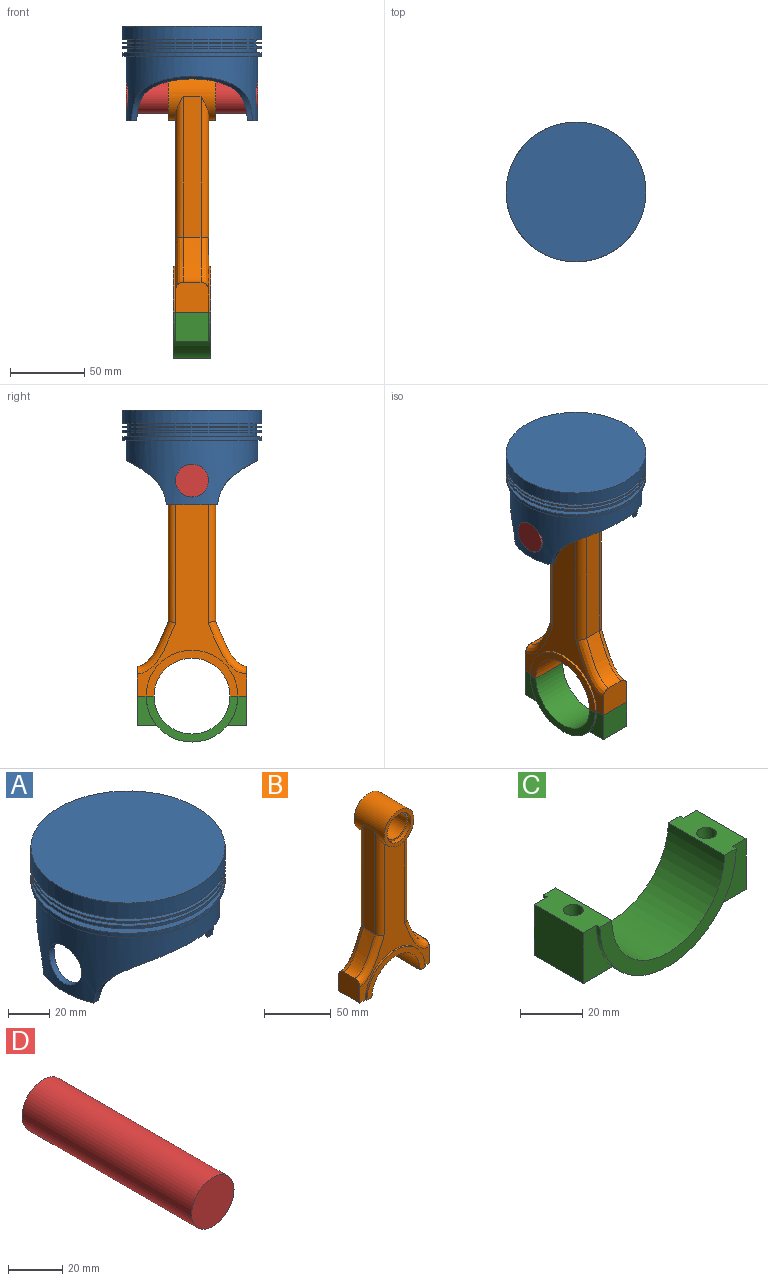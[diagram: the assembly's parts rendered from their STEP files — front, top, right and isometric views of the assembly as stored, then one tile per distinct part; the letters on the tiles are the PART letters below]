
ASSEMBLY  parts=4 mates=3
PART A: 24 faces, bbox 94x94x63.5 mm
  f0: cylinder r=44.12mm len=88.25mm, axis (0,0,1), area 6410.7mm2, adj f1,f2,f5,f20,f21,f22,f23
  f1: plane 34.12x6.9mm, normal (0,0,-1), area 111.5mm2, adj f0,f3,f20,f23
  f2: plane 34.12x6.9mm, normal (0,0,-1), area 111.5mm2, adj f0,f3,f20,f23
  f3: cylinder r=40.95mm len=81.9mm, axis (0,0,-1), area 9030.3mm2, adj f1,f2,f19,f20,f21,f22,f23
  f4: cylinder r=46.99mm len=93.98mm, axis (0,0,-1), area 712.8mm2, adj f5,f7
  f5: plane 93.98x93.98mm, normal (0,0,-1), area 820.3mm2, adj f0,f4
  f6: plane 93.98x93.98mm, normal (0,0,-1), area 1021.2mm2, adj f8,f9
  f7: plane 93.98x93.98mm, normal (0,0,1), area 1021.2mm2, adj f4,f8
  f8: cylinder r=43.39mm len=86.79mm, axis (0,0,-1), area 735mm2, adj f6,f7
  f9: cylinder r=46.99mm len=93.98mm, axis (0,0,-1), area 449.9mm2, adj f6,f11
  f10: plane 93.98x93.98mm, normal (0,0,-1), area 1021.2mm2, adj f12,f13
  f11: plane 93.98x93.98mm, normal (0,0,1), area 1021.2mm2, adj f9,f12
  f12: cylinder r=43.39mm len=86.79mm, axis (0,0,-1), area 463.4mm2, adj f10,f11
  f13: cylinder r=46.99mm len=93.98mm, axis (0,0,-1), area 328.8mm2, adj f10,f15
  f14: plane 93.98x93.98mm, normal (0,0,-1), area 1021.2mm2, adj f16,f18
  f15: plane 93.98x93.98mm, normal (0,0,1), area 1021.2mm2, adj f13,f16
  f16: cylinder r=43.39mm len=86.79mm, axis (0,0,-1), area 447.4mm2, adj f14,f15
  f17: plane 93.98x93.98mm, normal (0,0,1), area 6936.8mm2, adj f18
  f18: cylinder r=46.99mm len=93.98mm, axis (0,0,-1), area 2718.4mm2, adj f14,f17
  f19: plane 81.9x81.9mm, normal (0,0,-1), area 5268mm2, adj f3
  f20: extruded ~81.39x29.6mm, area 438.2mm2, adj f0,f1,f2,f3
  f21: cylinder r=11.01mm len=22.02mm, axis (1,0,0), area 223.6mm2, adj f0,f3
  f22: cylinder r=11.01mm len=22.02mm, axis (1,0,0), area 223.4mm2, adj f0,f3
  f23: extruded ~81.39x29.6mm, area 438.2mm2, adj f0,f1,f2,f3
PART B: 35 faces, bbox 79.2x31.9x160.8 mm
  f0: cylinder r=30.86mm len=61.72mm, axis (0,1,0), area 153.9mm2, adj f4,f12,f29,f30
  f1: cylinder r=12.7mm len=25.4mm, axis (0,1,0), area 253.4mm2, adj f17,f20
  f2: cylinder r=25.5mm len=51mm, axis (0,1,0), area 2034.3mm2, adj f4,f5,f29,f30
  f3: cylinder r=30.86mm len=61.72mm, axis (0,1,0), area 153.9mm2, adj f5,f13,f29,f30
  f4: plane 61.72x30.85mm, normal (0,-1,0), area 474.4mm2, adj f0,f2,f29,f30
  f5: plane 61.72x30.85mm, normal (0,1,0), area 474.4mm2, adj f2,f3,f29,f30
  f6: plane 94.46x12.07mm, normal (-1,0,0), area 1139.7mm2, adj f7,f15,f23,f27
  f7: extruded ~30.36x21.01mm, area 464.3mm2, adj f6,f8,f24,f28
  f8: plane 22.4x20.12mm, normal (-1,0,0), area 432.2mm2, adj f7,f12,f13,f24,f28,f29
  f9: plane 22.4x20.12mm, normal (1,0,0), area 432.2mm2, adj f10,f12,f13,f22,f26,f30
  f10: extruded ~30.36x21.01mm, area 464.3mm2, adj f9,f11,f22,f26
  f11: plane 94.46x12.07mm, normal (1,0,0), area 1139.7mm2, adj f10,f15,f21,f25
  f12: plane 133.13x73.78mm, normal (0,-1,0), area 2672.2mm2, adj f0,f8,f9,f15,f25,f26,f27,f28
  f13: plane 133.13x73.78mm, normal (0,1,0), area 2672.2mm2, adj f3,f8,f9,f15,f21,f22,f23,f24
  f14: cylinder r=12.7mm len=25.4mm, axis (0,1,0), area 253.4mm2, adj f16,f19
  f15: cylinder r=15.88mm len=31.75mm, axis (0,1,0), area 2191.2mm2, adj f6,f11,f12,f13,f16,f17,f21,f23
  f16: plane 31.75x31.75mm, normal (0,-1,0), area 285mm2, adj f14,f15
  f17: plane 31.75x31.75mm, normal (0,1,0), area 285mm2, adj f1,f15
  f18: cylinder r=11.01mm len=25.4mm, axis (0,1,0), area 1757.3mm2, adj f19,f20
  f19: plane 25.4x25.4mm, normal (0,-1,0), area 125.8mm2, adj f14,f18
  f20: plane 25.4x25.4mm, normal (0,1,0), area 125.8mm2, adj f1,f18
  f21: cylinder r=5.08mm len=95.44mm, axis (0,0,1), area 711.2mm2, adj f11,f13,f15,f22
  f22: bspline ~38.02x29.36mm, area 328.6mm2, adj f9,f10,f13,f21
  f23: cylinder r=5.08mm len=95.44mm, axis (0,0,-1), area 711.2mm2, adj f6,f13,f15,f24
  f24: bspline ~38.02x29.36mm, area 328.6mm2, adj f7,f8,f13,f23
  f25: cylinder r=5.08mm len=95.44mm, axis (0,0,-1), area 711.2mm2, adj f11,f12,f15,f26
  f26: bspline ~38.02x29.36mm, area 328.6mm2, adj f9,f10,f12,f25
  f27: cylinder r=5.08mm len=95.44mm, axis (0,0,1), area 711.2mm2, adj f6,f12,f15,f28
  f28: bspline ~38.02x29.36mm, area 328.6mm2, adj f7,f8,f12,f27
  f29: plane 25.4x11.38mm, normal (0,0,-1), area 238.3mm2, adj f0,f2,f3,f4,f5,f8,f12,f13
  f30: plane 25.4x11.38mm, normal (0,0,-1), area 238.3mm2, adj f0,f2,f3,f4,f5,f9,f12,f13
  f31: plane 6.35x6.35mm, normal (0,0,-1), area 31.7mm2, adj f32
  f32: cylinder r=3.17mm len=11.78mm, axis (0,0,-1), area 235mm2, adj f29,f31
  f33: plane 6.35x6.35mm, normal (0,0,-1), area 31.7mm2, adj f34
  f34: cylinder r=3.17mm len=11.78mm, axis (0,0,-1), area 235mm2, adj f30,f33
PART C: 16 faces, bbox 73.8x25.4x30.8 mm
  f0: plane 19.95x13.34mm, normal (0,1,0), area 166.2mm2, adj f2,f8,f12,f15
  f1: plane 19.95x13.34mm, normal (0,-1,0), area 166.2mm2, adj f2,f8,f12,f15
  f2: plane 22.23x19.95mm, normal (1,0,0), area 443.3mm2, adj f0,f1,f12,f15
  f3: plane 61.72x30.85mm, normal (0,1,0), area 474.4mm2, adj f8,f9,f14,f15
  f4: plane 19.95x13.34mm, normal (0,1,0), area 166.2mm2, adj f6,f8,f10,f14
  f5: plane 19.95x13.34mm, normal (0,-1,0), area 166.2mm2, adj f6,f8,f10,f14
  f6: plane 22.23x19.95mm, normal (-1,0,0), area 443.3mm2, adj f4,f5,f10,f14
  f7: plane 61.72x30.85mm, normal (0,-1,0), area 474.4mm2, adj f8,f9,f14,f15
  f8: cylinder r=30.86mm len=61.72mm, axis (0,1,0), area 1497.8mm2, adj f0,f1,f3,f4,f5,f7,f10,f12
  f9: cylinder r=25.5mm len=51mm, axis (0,1,0), area 2034.3mm2, adj f3,f7,f14,f15
  f10: plane 22.23x13.34mm, normal (0,0,-1), area 264.9mm2, adj f4,f5,f6,f8,f11
  f11: cylinder r=3.17mm len=19.95mm, axis (0,0,-1), area 397.9mm2, adj f10,f14
  f12: plane 22.23x13.34mm, normal (0,0,-1), area 264.9mm2, adj f0,f1,f2,f8,f13
  f13: cylinder r=3.17mm len=19.95mm, axis (0,0,-1), area 397.9mm2, adj f12,f15
  f14: plane 25.4x11.38mm, normal (0,0,1), area 238.3mm2, adj f3,f4,f5,f6,f7,f8,f9,f11
  f15: plane 25.4x11.38mm, normal (0,0,1), area 238.3mm2, adj f0,f1,f2,f3,f7,f8,f9,f13
PART D: 3 faces, bbox 22x88.3x22 mm
  f0: cylinder r=11.01mm len=88.27mm, axis (0,1,0), area 6106.5mm2, adj f1,f2
  f1: plane 22.02x22.02mm, normal (0,-1,0), area 380.9mm2, adj f0
  f2: plane 22.02x22.02mm, normal (0,1,0), area 380.9mm2, adj f0
PLACE A t=(-36.93,2.48,3.96)mm
PLACE B rot(axis=(0,0,1),90deg) t=(-36.89,2.48,-124.8)mm
PLACE C rot(axis=(0,0,-1),90deg) t=(-36.89,2.48,-124.77)mm
PLACE D rot(axis=(-0.58,0.58,0.58),120deg) t=(-81.03,2.48,19.98)mm
MATE fastened C.f11 <-> B.f34  axis (0,0,1) through (-36.89,32.67,-124.78)mm
MATE revolute B.f1 <-> D.f0  axis (-1,0,0) through (-36.89,2.48,19.98)mm
MATE fastened D.f0 <-> A.f21  axis (1,0,0) through (7.24,2.48,19.98)mm
